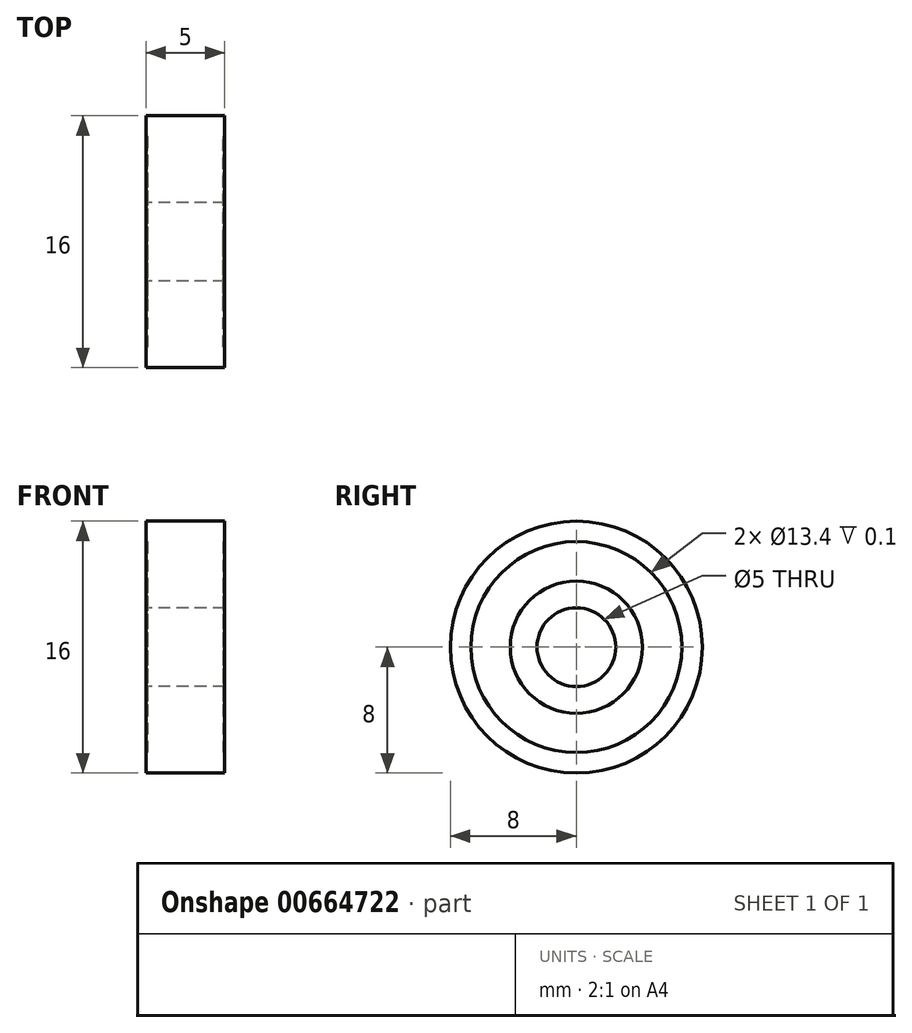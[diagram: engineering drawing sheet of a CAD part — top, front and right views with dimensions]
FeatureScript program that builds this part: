
annotation { "Feature Type Name" : "Feature", "Feature Type Description" : "" }
export const myFeature = defineFeature(function(context is Context, id is Id, definition is map)
    precondition{}
    {
        {
            var Q0;
            Q0=qCreatedBy(makeId("Front.planeOp"),FACE);
            var sketch = newSketch(context, id + "F0", { "sketchPlane" : qUnion([Q0])});
            skLineSegment(sketch, "E0", {"start": v(-7.35, 0) * mm, "end": v(8.68, 0) * mm, "construction": true});
            skLineSegment(sketch, "E1", {"start": v(0, 0) * mm, "end": v(0, 15.4) * mm, "construction": true});
            skLineSegment(sketch, "E2.0", {"start": v(-7.35, 2.5) * mm, "end": v(8.68, 2.5) * mm, "construction": true});
            skLineSegment(sketch, "E3.0", {"start": v(-7.35, 4.2) * mm, "end": v(8.68, 4.2) * mm, "construction": true});
            skLineSegment(sketch, "E4.0", {"start": v(-2.2, 8) * mm, "end": v(2.2, 8) * mm, "construction": true});
            skLineSegment(sketch, "E5.0", {"start": v(2.5, 0) * mm, "end": v(2.5, 7.7) * mm, "construction": true});
            skLineSegment(sketch, "E6.0", {"start": v(-2.5, 0) * mm, "end": v(-2.5, 7.7) * mm, "construction": true});
            skLineSegment(sketch, "E7.0", {"start": v(-7.35, 6.7) * mm, "end": v(8.68, 6.7) * mm, "construction": true});
            skLineSegment(sketch, "E8.0", {"start": v(-3.43, 0) * mm, "end": v(-3.43, 15.4) * mm, "construction": true});
            skLineSegment(sketch, "E9", {"start": v(-2.5, 2.5) * mm, "end": v(-2.5, 4.2) * mm});
            skLineSegment(sketch, "E10", {"start": v(-2.5, 4.2) * mm, "end": v(-2.4, 4.2) * mm});
            skLineSegment(sketch, "E11", {"start": v(-2.4, 4.2) * mm, "end": v(-2.4, 6.7) * mm});
            skLineSegment(sketch, "E12", {"start": v(-2.4, 6.7) * mm, "end": v(-2.5, 6.7) * mm});
            skLineSegment(sketch, "E13", {"start": v(-2.5, 6.7) * mm, "end": v(-2.5, 8) * mm});
            skLineSegment(sketch, "E14", {"start": v(-2.5, 8) * mm, "end": v(2.5, 8) * mm});
            skLineSegment(sketch, "E15", {"start": v(2.5, 8) * mm, "end": v(2.5, 6.7) * mm});
            skLineSegment(sketch, "E16", {"start": v(2.5, 6.7) * mm, "end": v(2.4, 6.7) * mm});
            skLineSegment(sketch, "E17", {"start": v(2.4, 6.7) * mm, "end": v(2.4, 4.2) * mm});
            skLineSegment(sketch, "E18", {"start": v(2.4, 4.2) * mm, "end": v(2.5, 4.2) * mm});
            skLineSegment(sketch, "E19", {"start": v(2.5, 4.2) * mm, "end": v(2.5, 2.5) * mm});
            skLineSegment(sketch, "E20", {"start": v(2.5, 2.5) * mm, "end": v(-2.5, 2.5) * mm});
            skArc(sketch, "E21.filletArc", {"start": v(-2.2, 8) * mm, "mid": v(-2.41, 7.91) * mm, "end": v(-2.5, 7.7) * mm, "construction": true});
            skArc(sketch, "E22.filletArc", {"start": v(2.5, 7.7) * mm, "mid": v(2.41, 7.91) * mm, "end": v(2.2, 8) * mm, "construction": true});
            skSolve(sketch);
        }
        {
            var Q0;
            Q0 = qSketchRegion(id + "F0", true);
            var Q1;
            Q1=sQuery(id+"F0.wireOp",EDGE,"E0");
            revolve(context, id + "F1", {"entities" : qUnion([Q0]), "axis" : qUnion([Q1]), "revolveType" : RevolveType.FULL});
        }
    });
